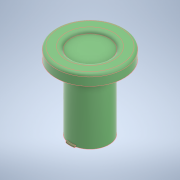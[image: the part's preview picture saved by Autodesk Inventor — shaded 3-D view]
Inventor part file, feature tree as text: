
AUTODESK INVENTOR PART (.ipt)
format: ipt  version: 2022 (Build 260153000, 153)  size: 176,640 bytes
history: native  units: mm
features: sketch x3, extrude x2, fillet x2, revolve x1
ambient origin geometry x8: Origin, YZ Plane, XZ Plane, XY Plane, X Axis, Y Axis, Z Axis, Center Point
bodies: Solid1 (feature_tree)
feature tree (8):
  revolve  "Revolution1"  [1 undecoded]
  extrude  "Extrusion1"  Depth=1.0mm
  fillet  "Fillet1"  Radius=14.0mm
  fillet  "Fillet2"  [1 undecoded]
  extrude  "Extrusion2"  Depth=1.0mm TaperAngle=0.0deg
  sketch  "Sketch2"  dims[d0=4.0mm d2=25.0mm]
  sketch  "Sketch3"  dims[d3=28.0mm d4=1.0mm d5=14.0mm d6=90.0deg]
  sketch  "Sketch4"  dims[d7=14.0mm d8=1.0mm d9=0.0mm d10=2.0mm d11=1.0mm d12=0.5mm d13=1.584493mm d14=1.584493mm d15=1.584493mm d16=1.584493mm d17=0.5mm d18=0.0mm]
note: 2 required parameter values undecoded (feature->parameter linkage not recoverable at this tier; creation-order binding heuristic only, values carry confidence <= 0.55)